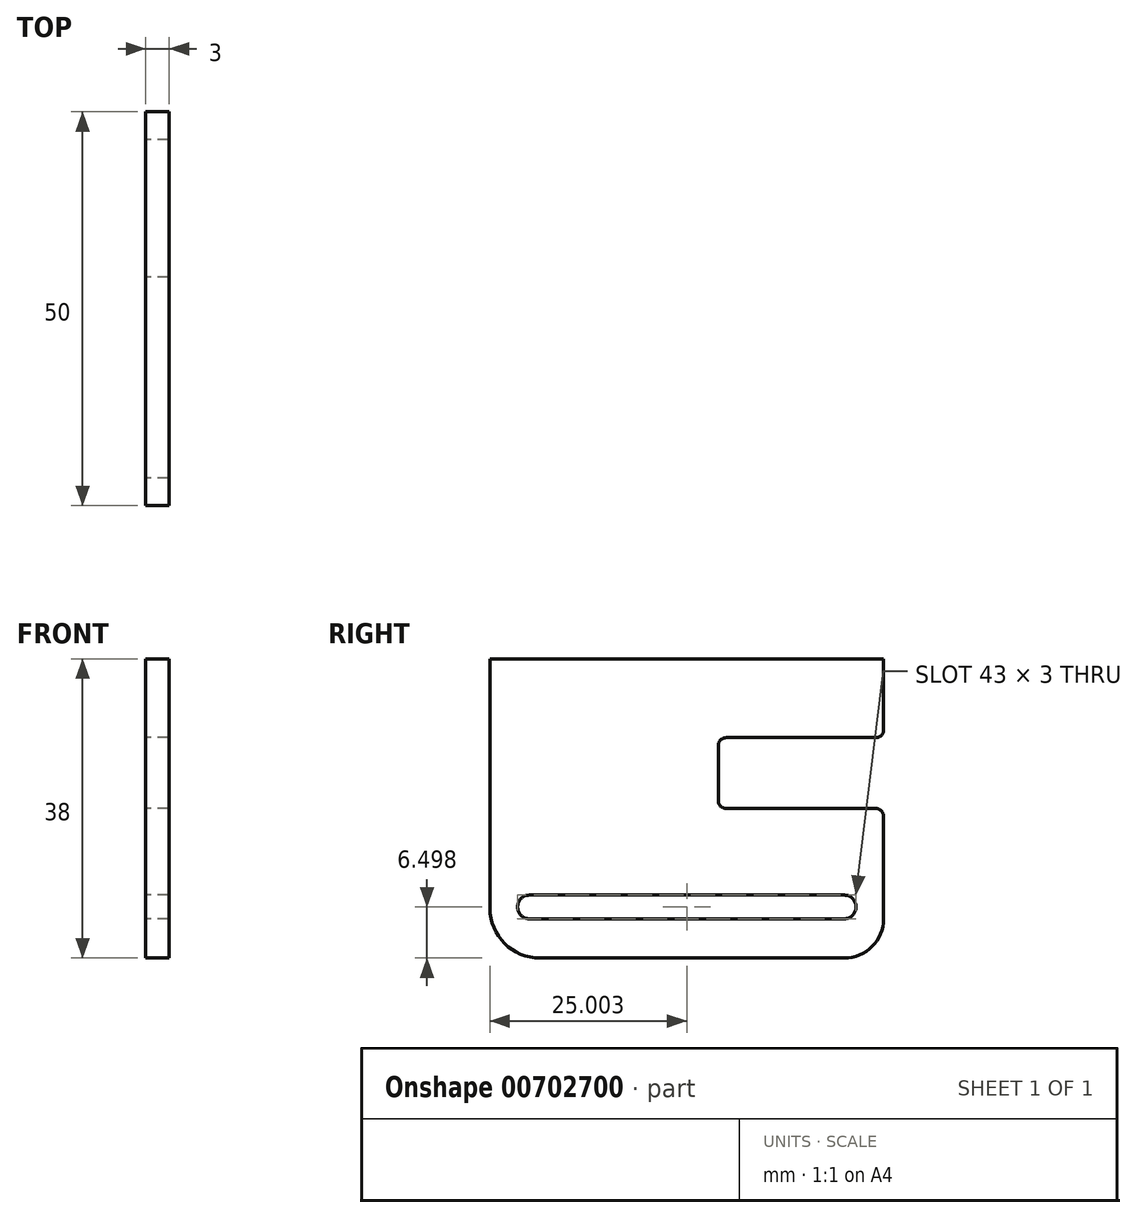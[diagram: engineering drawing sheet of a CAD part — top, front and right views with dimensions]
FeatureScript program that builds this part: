
annotation { "Feature Type Name" : "Feature", "Feature Type Description" : "" }
export const myFeature = defineFeature(function(context is Context, id is Id, definition is map)
    precondition{}
    {
        {
            var Q0;
            Q0=qCreatedBy(makeId("Right.planeOp"),FACE);
            var sketch = newSketch(context, id + "F0", { "sketchPlane" : qUnion([Q0])});
            skLineSegment(sketch, "E0", {"start": v(-25.7, 18.1) * mm, "end": v(24.3, 18.1) * mm});
            skLineSegment(sketch, "E1", {"start": v(24.3, 18.1) * mm, "end": v(24.3, 9.1) * mm});
            skLineSegment(sketch, "E2", {"start": v(23.3, 8.1) * mm, "end": v(4.3, 8.1) * mm});
            skLineSegment(sketch, "E3", {"start": v(3.3, 7.1) * mm, "end": v(3.3, 0.1) * mm});
            skLineSegment(sketch, "E4", {"start": v(4.3, -0.9) * mm, "end": v(23.3, -0.9) * mm});
            skLineSegment(sketch, "E5", {"start": v(24.3, -1.9) * mm, "end": v(24.3, -14.9) * mm});
            skLineSegment(sketch, "E6", {"start": v(19.3, -19.9) * mm, "end": v(-19.35, -19.9) * mm});
            skLineSegment(sketch, "E7", {"start": v(-25.7, -13.55) * mm, "end": v(-25.7, 18.1) * mm});
            skArc(sketch, "E8", {"start": v(-20.7, -11.9) * mm, "mid": v(-22.2, -13.4) * mm, "end": v(-20.7, -14.9) * mm});
            skArc(sketch, "E9", {"start": v(19.3, -14.9) * mm, "mid": v(20.8, -13.4) * mm, "end": v(19.3, -11.9) * mm});
            skPoint(sketch, "E10.orphan", {"position": v(-25.7, -13.4) * mm});
            skLineSegment(sketch, "E11.0", {"start": v(-20.7, -14.9) * mm, "end": v(19.3, -14.9) * mm});
            skLineSegment(sketch, "E12.0", {"start": v(-20.7, -11.9) * mm, "end": v(19.3, -11.9) * mm});
            skPoint(sketch, "E13.visualSharp", {"position": v(-25.7, -19.9) * mm});
            skArc(sketch, "E13.filletArc", {"start": v(-25.7, -13.55) * mm, "mid": v(-23.84, -18.04) * mm, "end": v(-19.35, -19.9) * mm});
            skPoint(sketch, "E14.visualSharp", {"position": v(24.3, -19.9) * mm});
            skArc(sketch, "E14.filletArc", {"start": v(19.3, -19.9) * mm, "mid": v(22.84, -18.44) * mm, "end": v(24.3, -14.9) * mm});
            skPoint(sketch, "E15.visualSharp", {"position": v(24.3, 8.1) * mm});
            skArc(sketch, "E15.filletArc", {"start": v(23.3, 8.1) * mm, "mid": v(24, 8.4) * mm, "end": v(24.3, 9.1) * mm});
            skPoint(sketch, "E16.visualSharp", {"position": v(3.3, 8.1) * mm});
            skArc(sketch, "E16.filletArc", {"start": v(4.3, 8.1) * mm, "mid": v(3.6, 7.8) * mm, "end": v(3.3, 7.1) * mm});
            skPoint(sketch, "E17.visualSharp", {"position": v(3.3, -0.9) * mm});
            skArc(sketch, "E17.filletArc", {"start": v(3.3, 0.1) * mm, "mid": v(3.6, -0.6) * mm, "end": v(4.3, -0.9) * mm});
            skPoint(sketch, "E18.visualSharp", {"position": v(24.3, -0.9) * mm});
            skArc(sketch, "E18.filletArc", {"start": v(24.3, -1.9) * mm, "mid": v(24, -1.2) * mm, "end": v(23.3, -0.9) * mm});
            skSolve(sketch);
        }
        {
            var Q0;
            Q0=makeQuery(id+"F0.imprint","IMPRINT",FACE,{"disambiguationData":[TD([[makeQuery(id+"F0.imprint","IMPRINT",EDGE,{"derivedFrom":sQuery(id+"F0.wireOp",EDGE,"E0")}),-1.0]])]});
            extrude(context, id + "F1", {"entities" : qUnion([Q0]), "depth" : 3 * mm, "offsetDistance" : 25.4 * mm});
        }
    });
